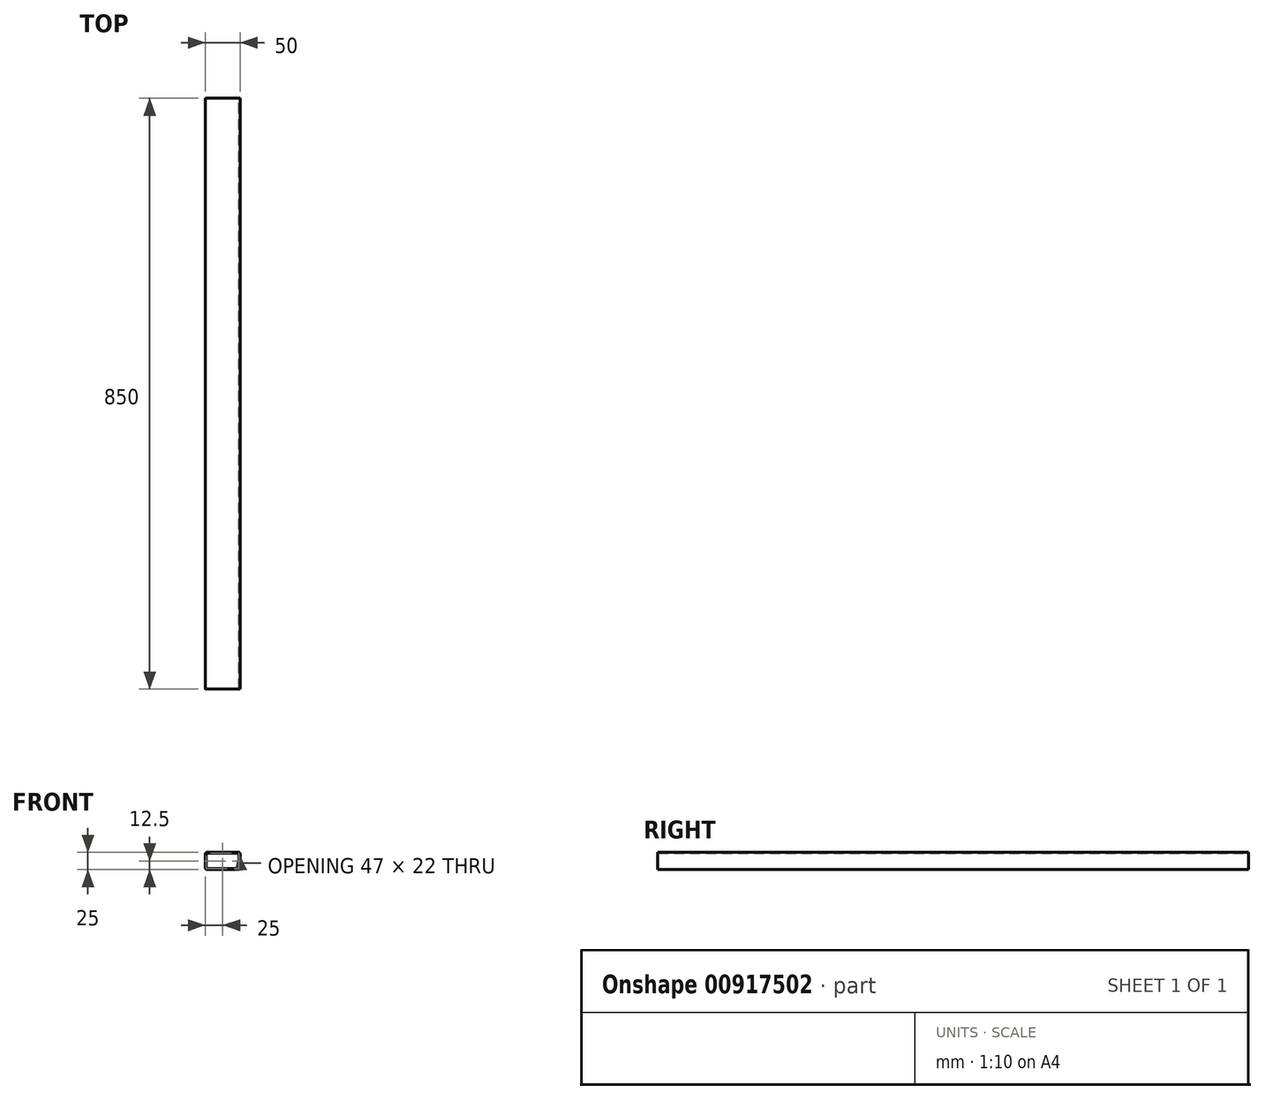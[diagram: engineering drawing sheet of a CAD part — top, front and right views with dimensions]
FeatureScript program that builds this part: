
annotation { "Feature Type Name" : "Feature", "Feature Type Description" : "" }
export const myFeature = defineFeature(function(context is Context, id is Id, definition is map)
    precondition{}
    {
        {
            var Q0;
            Q0=qCreatedBy(makeId("Front.planeOp"),FACE);
            var sketch = newSketch(context, id + "F0", { "sketchPlane" : qUnion([Q0])});
            skLineSegment(sketch, "E0.bottom", {"start": v(22.5, 12.5) * mm, "end": v(-22.5, 12.5) * mm});
            skLineSegment(sketch, "E0.top", {"start": v(22.5, -12.5) * mm, "end": v(-22.5, -12.5) * mm});
            skLineSegment(sketch, "E0.left", {"start": v(25, 10) * mm, "end": v(25, -10) * mm});
            skLineSegment(sketch, "E0.right", {"start": v(-25, 10) * mm, "end": v(-25, -10) * mm});
            skPoint(sketch, "E0.middle", {"position": v(0, 0) * mm});
            skPoint(sketch, "E1.visualSharp", {"position": v(25, 12.5) * mm});
            skArc(sketch, "E1.filletArc", {"start": v(25, 10) * mm, "mid": v(24.27, 11.77) * mm, "end": v(22.5, 12.5) * mm});
            skPoint(sketch, "E2.visualSharp", {"position": v(25, -12.5) * mm});
            skArc(sketch, "E2.filletArc", {"start": v(22.5, -12.5) * mm, "mid": v(24.27, -11.77) * mm, "end": v(25, -10) * mm});
            skPoint(sketch, "E3.visualSharp", {"position": v(-25, -12.5) * mm});
            skArc(sketch, "E3.filletArc", {"start": v(-25, -10) * mm, "mid": v(-24.27, -11.77) * mm, "end": v(-22.5, -12.5) * mm});
            skPoint(sketch, "E4.visualSharp", {"position": v(-25, 12.5) * mm});
            skArc(sketch, "E4.filletArc", {"start": v(-22.5, 12.5) * mm, "mid": v(-24.27, 11.77) * mm, "end": v(-25, 10) * mm});
            skLineSegment(sketch, "E5.0", {"start": v(23.5, 10) * mm, "end": v(23.5, -10) * mm});
            skLineSegment(sketch, "E5.1", {"start": v(22.5, 11) * mm, "end": v(-22.5, 11) * mm});
            skLineSegment(sketch, "E5.2", {"start": v(-23.5, 10) * mm, "end": v(-23.5, -10) * mm});
            skLineSegment(sketch, "E5.3", {"start": v(22.5, -11) * mm, "end": v(-22.5, -11) * mm});
            skPoint(sketch, "E6.visualSharp", {"position": v(-23.5, 11) * mm});
            skArc(sketch, "E6.filletArc", {"start": v(-22.5, 11) * mm, "mid": v(-23.2, 10.7) * mm, "end": v(-23.5, 10) * mm});
            skPoint(sketch, "E7.visualSharp", {"position": v(-23.5, -11) * mm});
            skArc(sketch, "E7.filletArc", {"start": v(-23.5, -10) * mm, "mid": v(-23.2, -10.7) * mm, "end": v(-22.5, -11) * mm});
            skPoint(sketch, "E8.visualSharp", {"position": v(23.5, -11) * mm});
            skArc(sketch, "E8.filletArc", {"start": v(22.5, -11) * mm, "mid": v(23.2, -10.7) * mm, "end": v(23.5, -10) * mm});
            skPoint(sketch, "E9.visualSharp", {"position": v(23.5, 11) * mm});
            skArc(sketch, "E9.filletArc", {"start": v(23.5, 10) * mm, "mid": v(23.2, 10.7) * mm, "end": v(22.5, 11) * mm});
            skSolve(sketch);
        }
        {
            var Q0;
            Q0=qSketchRegion(id+"F0",true);
            extrude(context, id + "F1", {"entities" : qUnion([Q0]), "depth" : 850 * mm, "offsetDistance" : 25 * mm, "symmetric" : true});
        }
    });
